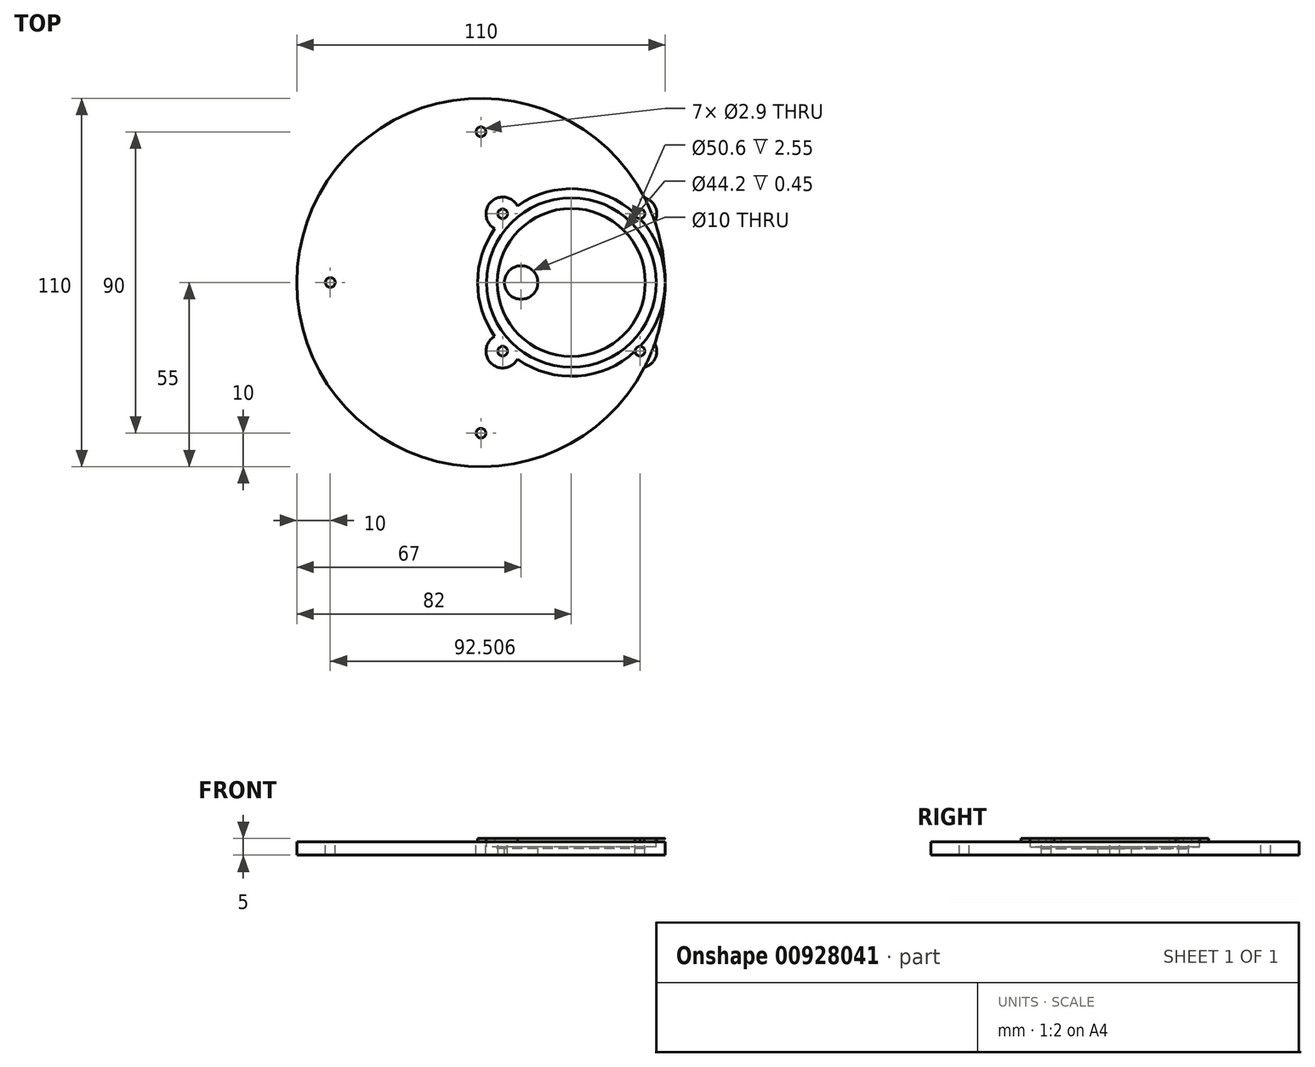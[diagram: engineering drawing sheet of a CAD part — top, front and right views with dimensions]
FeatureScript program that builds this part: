
annotation { "Feature Type Name" : "Feature", "Feature Type Description" : "" }
export const myFeature = defineFeature(function(context is Context, id is Id, definition is map)
    precondition{}
    {
        {
            var Q0;
            Q0=qCreatedBy(makeId("Top.planeOp"),FACE);
            var sketch = newSketch(context, id + "F0", { "sketchPlane" : qUnion([Q0])});
            skCircle(sketch, "E0", {"center": v(0, 0) * mm, "radius": 55 * mm});
            skSolve(sketch);
        }
        {
            var Q0;
            Q0=makeQuery(id+"F0.imprint","IMPRINT",FACE,{"disambiguationData":[TD([[makeQuery(id+"F0.imprint","IMPRINT",EDGE,{"derivedFrom":sQuery(id+"F0.wireOp",EDGE,"E0")}),1.0]])]});
            extrude(context, id + "F1", {"entities" : qUnion([Q0]), "depth" : 4 * mm, "offsetDistance" : 25 * mm});
        }
        {
            var Q0;
            Q0=makeQuery(id+"F1.opExtrude","CAP_FACE",FACE,{"disambiguationData":[OSD([sQuery(id+"F0.wireOp",EDGE,"E0")])],"isStart":false});
            var sketch = newSketch(context, id + "F2", { "sketchPlane" : qUnion([Q0])});
            skCircle(sketch, "E1", {"center": v(27, 0) * mm, "radius": 22.1 * mm});
            skSolve(sketch);
        }
        {
            var Q0;
            Q0=makeQuery(id+"F2.imprint","IMPRINT",FACE,{"disambiguationData":[TD([[makeQuery(id+"F2.imprint","IMPRINT",EDGE,{"derivedFrom":sQuery(id+"F2.wireOp",EDGE,"E1")}),1.0]])]});
            extrude(context, id + "F3", {"entities" : qUnion([Q0]), "operationType" : NewBodyOperationType.REMOVE, "oppositeDirection" : true, "depth" : 2 * mm, "offsetDistance" : 25 * mm});
        }
        {
            var Q0;
            Q0=makeQuery(id+"F1.opExtrude","CAP_FACE",FACE,{"disambiguationData":[OSD([sQuery(id+"F0.wireOp",EDGE,"E0")])],"isStart":false});
            var sketch = newSketch(context, id + "F4", { "sketchPlane" : qUnion([Q0])});
            skCircle(sketch, "E2", {"center": v(27, 0) * mm, "radius": 25.3 * mm});
            skSolve(sketch);
        }
        {
            var Q0;
            Q0=makeQuery(id+"F4.imprint","IMPRINT",FACE,{"disambiguationData":[TD([[makeQuery(id+"F4.imprint","IMPRINT",EDGE,{"derivedFrom":sQuery(id+"F4.wireOp",EDGE,"E2")}),1.0]])]});
            extrude(context, id + "F5", {"entities" : qUnion([Q0]), "operationType" : NewBodyOperationType.REMOVE, "oppositeDirection" : true, "depth" : 1.55 * mm, "offsetDistance" : 25 * mm});
        }
        {
            var Q0;
            Q0=makeQuery(id+"F1.opExtrude","CAP_FACE",FACE,{"disambiguationData":[OSD([sQuery(id+"F0.wireOp",EDGE,"E0")])],"isStart":false});
            var sketch = newSketch(context, id + "F6", { "sketchPlane" : qUnion([Q0])});
            skCircle(sketch, "E3", {"center": v(27, 0) * mm, "radius": 28 * mm});
            skSolve(sketch);
        }
        {
            var Q0;
            Q0=makeQuery(id+"F6.imprint","IMPRINT",FACE,{"disambiguationData":[TD([[makeQuery(id+"F6.imprint","IMPRINT",EDGE,{"derivedFrom":sQuery(id+"F6.wireOp",EDGE,"E3")}),1.0]])]});
            extrude(context, id + "F7", {"entities" : qUnion([Q0]), "operationType" : NewBodyOperationType.ADD, "depth" : 1 * mm, "offsetDistance" : 25 * mm});
        }
        {
            var Q0;
            Q0=makeQuery(id+"F3.boolean.opBoolean","COPY",FACE,{"derivedFrom":makeQuery(id+"F3.opExtrude","CAP_FACE",FACE,{"disambiguationData":[OSD([sQuery(id+"F2.wireOp",EDGE,"E1")])],"isStart":false})});
            var sketch = newSketch(context, id + "F8", { "sketchPlane" : qUnion([Q0])});
            skCircle(sketch, "E4", {"center": v(12, 0) * mm, "radius": 5 * mm});
            skSolve(sketch);
        }
        {
            var Q0;
            Q0=makeQuery(id+"F8.imprint","IMPRINT",FACE,{"disambiguationData":[TD([[makeQuery(id+"F8.imprint","IMPRINT",EDGE,{"derivedFrom":sQuery(id+"F8.wireOp",EDGE,"E4")}),1.0]])]});
            extrude(context, id + "F9", {"entities" : qUnion([Q0]), "operationType" : NewBodyOperationType.REMOVE, "oppositeDirection" : true, "depth" : 25 * mm, "offsetDistance" : 25 * mm});
        }
        {
            var Q0;
            Q0=makeQuery(id+"F1.opExtrude","CAP_FACE",FACE,{"disambiguationData":[OSD([sQuery(id+"F0.wireOp",EDGE,"E0")])],"isStart":false});
            var sketch = newSketch(context, id + "F10", { "sketchPlane" : qUnion([Q0])});
            skPoint(sketch, "E5", {"position": v(-2, 0) * mm});
            skPoint(sketch, "E6", {"position": v(27, 0) * mm});
            skCircle(sketch, "E7.1.0", {"center": v(6.5, -20.5) * mm, "radius": 5 * mm});
            skCircle(sketch, "E7.3.0", {"center": v(47.5, -20.5) * mm, "radius": 5 * mm});
            skCircle(sketch, "E8.1.5.0", {"center": v(47.5, 20.5) * mm, "radius": 5 * mm});
            skCircle(sketch, "E8.1.7.0", {"center": v(6.5, 20.5) * mm, "radius": 5 * mm});
            skSolve(sketch);
        }
        {
            var Q0;
            {var subQ0=sQuery(id+"F10.wireOp",EDGE,"E7.1.0");var subQ1=makeQuery(id+"F7.opExtrude","CAP_EDGE",EDGE,{"disambiguationData":[OSD([sQuery(id+"F6.wireOp",EDGE,"E3")])],"isStart":true});var subQ2=makeQuery(id+"F10.imprint","INTERSECT",VERTEX,{"disambiguationData":[OD(0.0)],"derivedFrom":[subQ1,subQ0]});Q0=makeQuery(id+"F10.imprint","IMPRINT",FACE,{"disambiguationData":[TD([[makeQuery(id+"F10.imprint","IMPRINT",EDGE,{"disambiguationData":[TD([[subQ2,1.0]])],"derivedFrom":subQ0}),1.0]])]});}
            var Q1;
            {var subQ0=sQuery(id+"F10.wireOp",EDGE,"E7.3.0");var subQ1=makeQuery(id+"F1.opExtrude","CAP_EDGE",EDGE,{"disambiguationData":[OSD([sQuery(id+"F0.wireOp",EDGE,"E0")])],"isStart":false});var subQ2=makeQuery(id+"F10.imprint","INTERSECT",VERTEX,{"disambiguationData":[OD(0.0)],"derivedFrom":[subQ1,subQ0]});Q1=makeQuery(id+"F10.imprint","IMPRINT",FACE,{"disambiguationData":[TD([[makeQuery(id+"F10.imprint","IMPRINT",EDGE,{"disambiguationData":[TD([[subQ2,1.0]])],"derivedFrom":subQ0}),1.0]])]});}
            var Q2;
            {var subQ0=sQuery(id+"F10.wireOp",EDGE,"E8.1.7.0");var subQ1=makeQuery(id+"F7.opExtrude","CAP_EDGE",EDGE,{"disambiguationData":[OSD([sQuery(id+"F6.wireOp",EDGE,"E3")])],"isStart":true});var subQ2=makeQuery(id+"F10.imprint","INTERSECT",VERTEX,{"disambiguationData":[OD(0.0)],"derivedFrom":[subQ1,subQ0]});Q2=makeQuery(id+"F10.imprint","IMPRINT",FACE,{"disambiguationData":[TD([[makeQuery(id+"F10.imprint","IMPRINT",EDGE,{"disambiguationData":[TD([[subQ2,-1.0]])],"derivedFrom":subQ0}),1.0]])]});}
            var Q3;
            {var subQ0=sQuery(id+"F10.wireOp",EDGE,"E8.1.5.0");var subQ1=makeQuery(id+"F1.opExtrude","CAP_EDGE",EDGE,{"disambiguationData":[OSD([sQuery(id+"F0.wireOp",EDGE,"E0")])],"isStart":false});var subQ2=makeQuery(id+"F10.imprint","INTERSECT",VERTEX,{"disambiguationData":[OD(0.0)],"derivedFrom":[subQ1,subQ0]});Q3=makeQuery(id+"F10.imprint","IMPRINT",FACE,{"disambiguationData":[TD([[makeQuery(id+"F10.imprint","IMPRINT",EDGE,{"disambiguationData":[TD([[subQ2,1.0]])],"derivedFrom":subQ0}),1.0]])]});}
            extrude(context, id + "F11", {"entities" : qUnion([Q0, Q1, Q2, Q3]), "operationType" : NewBodyOperationType.ADD, "depth" : 1 * mm, "offsetDistance" : 25 * mm});
        }
        {
            var Q0;
            {var subQ0=sQuery(id+"F6.wireOp",EDGE,"E3");var subQ1=sQuery(id+"F0.wireOp",EDGE,"E0");Q0=makeQuery(id+"F11.boolean.opBoolean","MERGE",FACE,{"derivedFrom":[makeQuery(id+"F7.opExtrude","CAP_FACE",FACE,{"disambiguationData":[OSD([sQuery(id+"F4.wireOp",EDGE,"E2"),subQ0])],"isStart":false}),makeQuery(id+"F11.opExtrude","CAP_FACE",FACE,{"disambiguationData":[OSD([subQ0,sQuery(id+"F10.wireOp",EDGE,"E7.1.0")])],"isStart":false}),makeQuery(id+"F11.opExtrude","CAP_FACE",FACE,{"disambiguationData":[OSD([subQ1,subQ0,sQuery(id+"F10.wireOp",EDGE,"E7.3.0")])],"isStart":false}),makeQuery(id+"F11.opExtrude","CAP_FACE",FACE,{"disambiguationData":[OSD([subQ1,subQ0,sQuery(id+"F10.wireOp",EDGE,"E8.1.5.0")])],"isStart":false}),makeQuery(id+"F11.opExtrude","CAP_FACE",FACE,{"disambiguationData":[OSD([subQ0,sQuery(id+"F10.wireOp",EDGE,"E8.1.7.0")])],"isStart":false})]});}
            var sketch = newSketch(context, id + "F12", { "sketchPlane" : qUnion([Q0])});
            skCircle(sketch, "E9", {"center": v(6.5, -20.5) * mm, "radius": 1.45 * mm});
            skCircle(sketch, "E10.1.0", {"center": v(47.5, -20.5) * mm, "radius": 1.45 * mm});
            skCircle(sketch, "E10.2.0", {"center": v(47.5, 20.5) * mm, "radius": 1.45 * mm});
            skCircle(sketch, "E10.3.0", {"center": v(6.5, 20.5) * mm, "radius": 1.45 * mm});
            skPoint(sketch, "E10.center", {"position": v(27, 0) * mm});
            skSolve(sketch);
        }
        {
            var Q0;
            Q0=makeQuery(id+"F12.imprint","IMPRINT",FACE,{"disambiguationData":[TD([[makeQuery(id+"F12.imprint","IMPRINT",EDGE,{"derivedFrom":sQuery(id+"F12.wireOp",EDGE,"E10.3.0")}),1.0]])]});
            var Q1;
            Q1=makeQuery(id+"F12.imprint","IMPRINT",FACE,{"disambiguationData":[TD([[makeQuery(id+"F12.imprint","IMPRINT",EDGE,{"derivedFrom":sQuery(id+"F12.wireOp",EDGE,"E10.2.0")}),1.0]])]});
            var Q2;
            Q2=makeQuery(id+"F12.imprint","IMPRINT",FACE,{"disambiguationData":[TD([[makeQuery(id+"F12.imprint","IMPRINT",EDGE,{"derivedFrom":sQuery(id+"F12.wireOp",EDGE,"E10.1.0")}),1.0]])]});
            var Q3;
            Q3=makeQuery(id+"F12.imprint","IMPRINT",FACE,{"disambiguationData":[TD([[makeQuery(id+"F12.imprint","IMPRINT",EDGE,{"derivedFrom":sQuery(id+"F12.wireOp",EDGE,"E9")}),1.0]])]});
            extrude(context, id + "F13", {"entities" : qUnion([Q0, Q1, Q2, Q3]), "operationType" : NewBodyOperationType.REMOVE, "oppositeDirection" : true, "depth" : 25 * mm, "offsetDistance" : 25 * mm});
        }
        {
            var Q0;
            {var subQ1=sQuery(id+"F0.wireOp",EDGE,"E0");Q0=makeQuery(id+"F11.boolean.opBoolean","SPLIT",FACE,{"disambiguationData":[TD([makeQuery(id+"F11.opExtrude","SWEPT_FACE",FACE,{"disambiguationData":[OSD([sQuery(id+"F10.wireOp",EDGE,"E7.1.0")])]})])],"derivedFrom":makeQuery(id+"F1.opExtrude","CAP_FACE",FACE,{"disambiguationData":[OSD([subQ1])],"isStart":false})});}
            var sketch = newSketch(context, id + "F14", { "sketchPlane" : qUnion([Q0])});
            skCircle(sketch, "E11", {"center": v(0, -45) * mm, "radius": 1.45 * mm});
            skCircle(sketch, "E12.1.0", {"center": v(45, 0) * mm, "radius": 1.45 * mm});
            skCircle(sketch, "E12.2.0", {"center": v(0, 45) * mm, "radius": 1.45 * mm});
            skCircle(sketch, "E12.3.0", {"center": v(-45, 0) * mm, "radius": 1.45 * mm});
            skPoint(sketch, "E12.center", {"position": v(0, 0) * mm});
            skSolve(sketch);
        }
        {
            var Q0;
            Q0=makeQuery(id+"F14.imprint","IMPRINT",FACE,{"disambiguationData":[TD([[makeQuery(id+"F14.imprint","IMPRINT",EDGE,{"derivedFrom":sQuery(id+"F14.wireOp",EDGE,"E12.2.0")}),1.0]])]});
            var Q1;
            Q1=makeQuery(id+"F14.imprint","IMPRINT",FACE,{"disambiguationData":[TD([[makeQuery(id+"F14.imprint","IMPRINT",EDGE,{"derivedFrom":sQuery(id+"F14.wireOp",EDGE,"E12.3.0")}),1.0]])]});
            var Q2;
            Q2=makeQuery(id+"F14.imprint","IMPRINT",FACE,{"disambiguationData":[TD([[makeQuery(id+"F14.imprint","IMPRINT",EDGE,{"derivedFrom":sQuery(id+"F14.wireOp",EDGE,"E11")}),1.0]])]});
            extrude(context, id + "F15", {"entities" : qUnion([Q0, Q1, Q2]), "operationType" : NewBodyOperationType.REMOVE, "oppositeDirection" : true, "depth" : 25 * mm, "offsetDistance" : 25 * mm});
        }
    });
